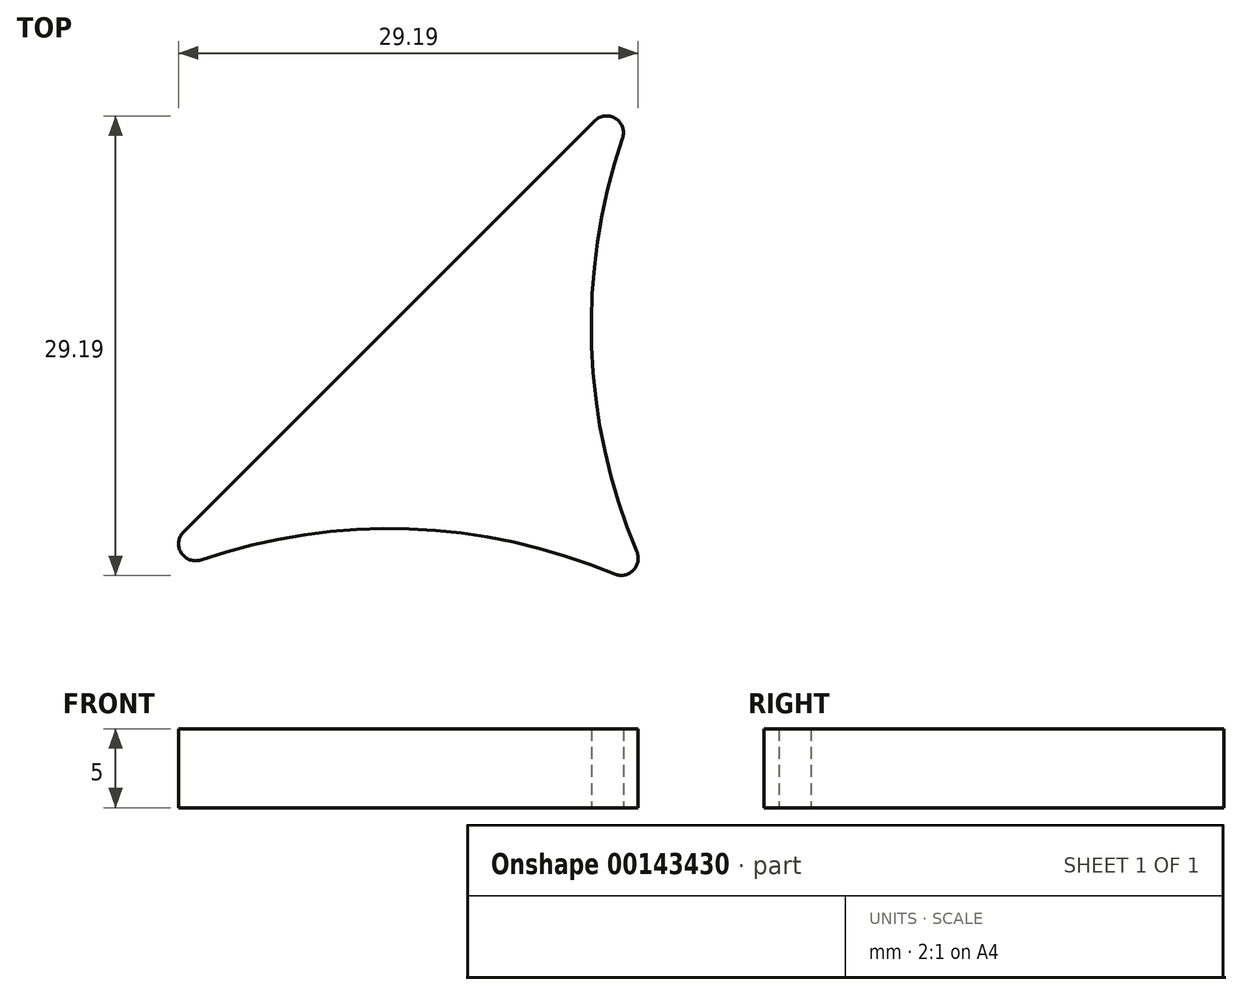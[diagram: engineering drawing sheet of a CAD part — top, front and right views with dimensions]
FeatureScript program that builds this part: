
annotation { "Feature Type Name" : "Feature", "Feature Type Description" : "" }
export const myFeature = defineFeature(function(context is Context, id is Id, definition is map)
    precondition{}
    {
        {
            var Q0;
            Q0=qCreatedBy(makeId("Top.planeOp"),FACE);
            var sketch = newSketch(context, id + "F0", { "sketchPlane" : qUnion([Q0])});
            skLineSegment(sketch, "E0", {"start": v(-15.65, 0) * mm, "end": v(18.3, 33.94) * mm});
            skArc(sketch, "E1", {"start": v(18.3, 0) * mm, "mid": v(1.32, 4.12) * mm, "end": v(-15.65, 0) * mm});
            skArc(sketch, "E2", {"start": v(18.3, 33.94) * mm, "mid": v(14.17, 16.97) * mm, "end": v(18.3, 0) * mm});
            skSolve(sketch);
        }
        {
            var Q0;
            Q0=makeQuery(id+"F0.imprint","IMPRINT",FACE,{"disambiguationData":[TD([[makeQuery(id+"F0.imprint","IMPRINT",EDGE,{"derivedFrom":sQuery(id+"F0.wireOp",EDGE,"E0")}),-1.0]])]});
            extrude(context, id + "F1", {"entities" : qUnion([Q0]), "depth" : 5 * mm});
        }
        {
            var Q0;
            Q0=makeQuery(id+"F1.opExtrude","SWEPT_EDGE",EDGE,{"disambiguationData":[OSD([sQuery(id+"F0.wireOp",EDGE,"E0"),sQuery(id+"F0.wireOp",EDGE,"E2")])]});
            var Q1;
            Q1=makeQuery(id+"F1.opExtrude","SWEPT_EDGE",EDGE,{"disambiguationData":[OSD([sQuery(id+"F0.wireOp",EDGE,"E0"),sQuery(id+"F0.wireOp",EDGE,"E1")])]});
            var Q2;
            Q2=makeQuery(id+"F1.opExtrude","SWEPT_EDGE",EDGE,{"disambiguationData":[OSD([sQuery(id+"F0.wireOp",EDGE,"E1"),sQuery(id+"F0.wireOp",EDGE,"E2")])]});
            fillet(context, id + "F2", {"entities" : qUnion([Q0, Q1, Q2]), "radius" : 1.07 * mm, "tangentPropagation" : true, "allowEdgeOverflow" : false});
        }
    });
